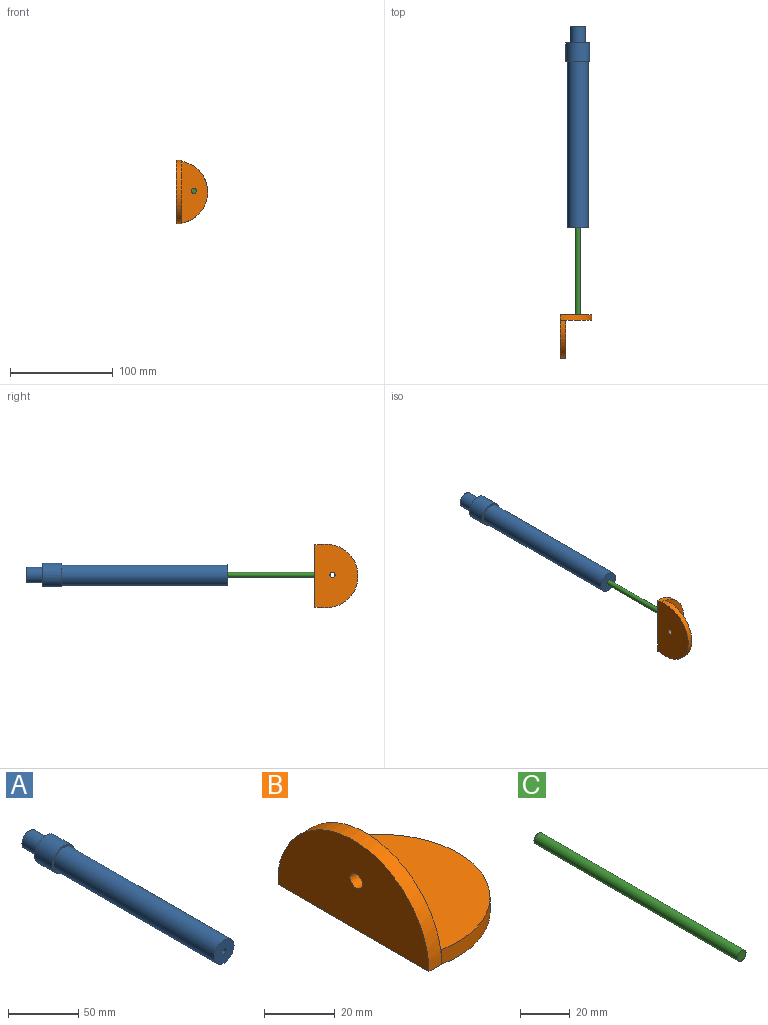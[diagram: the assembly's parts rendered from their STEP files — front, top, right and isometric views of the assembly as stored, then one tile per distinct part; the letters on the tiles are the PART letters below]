
ASSEMBLY  parts=3 mates=2
PART A: 9 faces, bbox 23x195.9x23 mm
  f0: cylinder r=10mm len=161.4mm, axis (0,1,0), area 10141.1mm2, adj f1,f3
  f1: plane 20x20mm, normal (0,-1,0), area 294.5mm2, adj f0,f2
  f2: cylinder r=2.5mm len=161.4mm, axis (0,-1,0), area 2535.3mm2, adj f1,f6
  f3: plane 23x23mm, normal (0,-1,0), area 101.3mm2, adj f0,f5
  f4: plane 23x23mm, normal (0,1,0), area 238.8mm2, adj f5,f7
  f5: cylinder r=11.5mm len=23mm, axis (0,-1,0), area 1300.6mm2, adj f3,f4
  f6: plane 5x5mm, normal (0,-1,0), area 19.6mm2, adj f2
  f7: cylinder r=7.5mm len=16.5mm, axis (0,1,0), area 777.5mm2, adj f4,f8
  f8: plane 15x15mm, normal (0,1,0), area 176.7mm2, adj f7
PART B: 11 faces, bbox 41.9x61.7x30.4 mm
  f0: plane 5.08x0.46mm, normal (-1,0,0), area 0.9mm2, adj f2,f3,f4,f5
  f1: plane 0.59x0.09mm, normal (-1,0,0), area 0mm2, adj f2,f3,f5
  f2: cylinder r=30.84mm len=61.68mm, axis (0,0,-1), area 553.4mm2, adj f0,f1,f3,f4,f6
  f3: plane 61.68x36.83mm, normal (0,0,1), area 1841.1mm2, adj f0,f1,f2,f8,f9
  f4: plane 61.68x41.91mm, normal (0,0,-1), area 2148.3mm2, adj f0,f2,f5,f6,f7,f9
  f5: cylinder r=30.4mm len=60.47mm, axis (1,0,0), area 462.3mm2, adj f0,f1,f4,f6,f7,f8
  f6: plane 5.08x4.49mm, normal (0,1,0), area 22.8mm2, adj f2,f4,f5,f7
  f7: plane 60.47x30.4mm, normal (-1,0,0), area 1431.2mm2, adj f4,f5,f6,f10
  f8: plane 59.95x25.32mm, normal (1,0,0), area 1124.7mm2, adj f3,f5,f10
  f9: cylinder r=2.5mm len=5.08mm, axis (0,0,1), area 79.9mm2, adj f3,f4
  f10: cylinder r=2.5mm len=5.08mm, axis (1,0,0), area 79.9mm2, adj f7,f8
PART C: 3 faces, bbox 5x115x5 mm
  f0: cylinder r=2.5mm len=115mm, axis (0,1,0), area 1806.4mm2, adj f1,f2
  f1: plane 5x5mm, normal (0,-1,0), area 19.6mm2, adj f0
  f2: plane 5x5mm, normal (0,1,0), area 19.6mm2, adj f0
PLACE A t=(360.48,311.76,15.52)mm
PLACE B rot(axis=(-0.58,0.58,-0.58),120deg) t=(290.52,85.83,40.98)mm
PLACE C t=(361.39,205.91,3.47)mm
MATE slider A.f0 <-> C.f0  axis (0,-1,0) through (307.38,337.16,40.98)mm
MATE fastened B.f10 <-> C.f0  axis (0,1,0) through (307.38,90.91,40.98)mm
